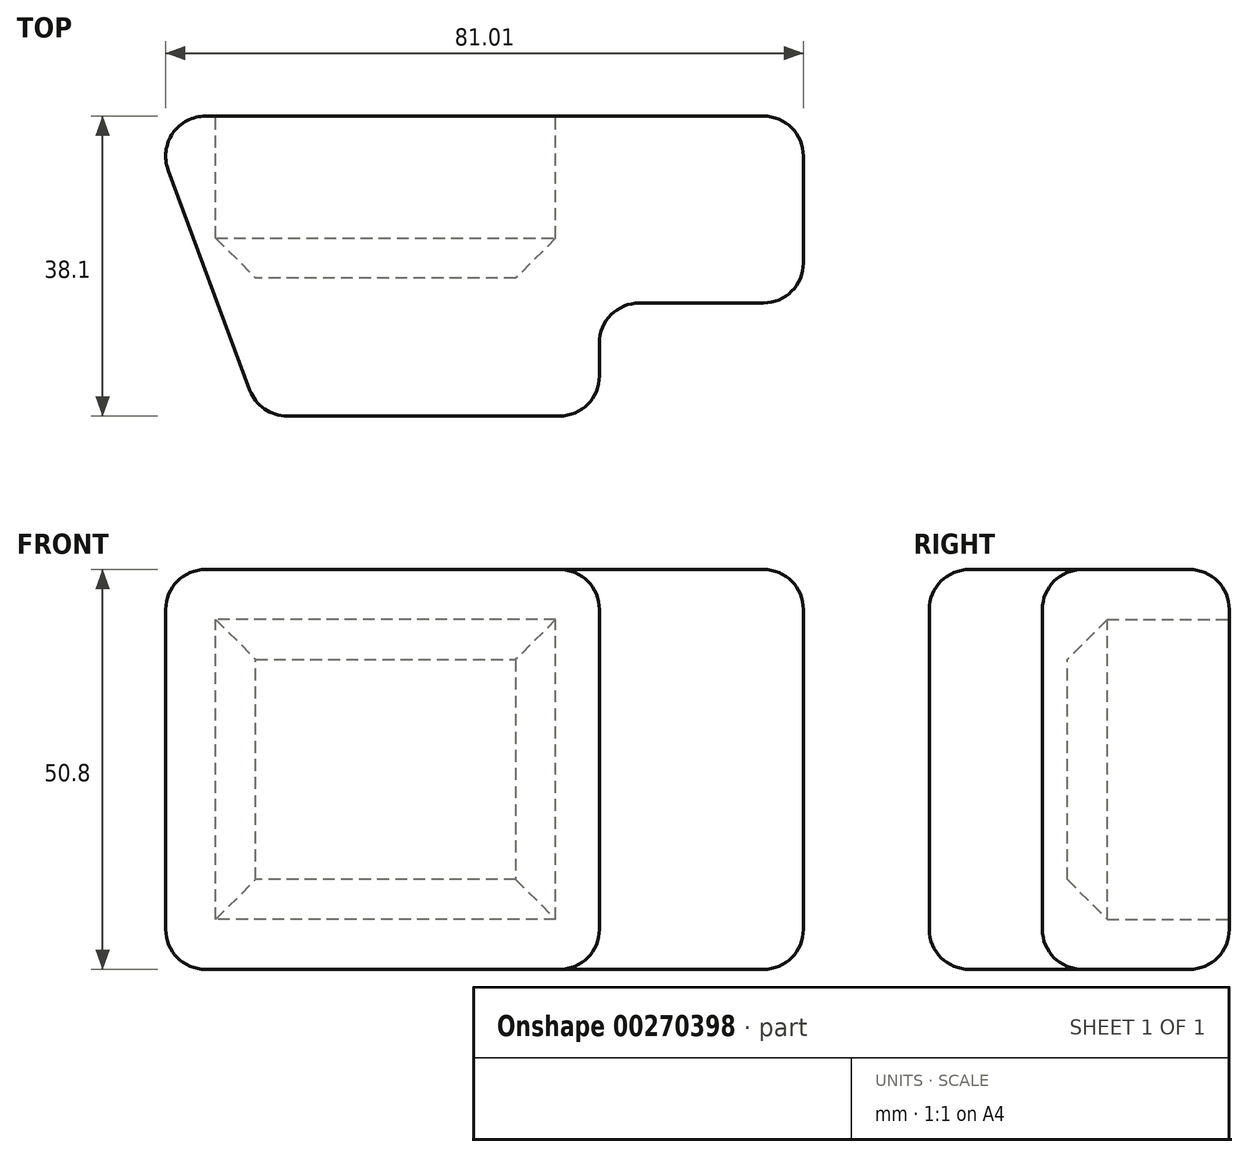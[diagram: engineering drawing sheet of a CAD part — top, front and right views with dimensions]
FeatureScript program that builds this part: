
annotation { "Feature Type Name" : "Feature", "Feature Type Description" : "" }
export const myFeature = defineFeature(function(context is Context, id is Id, definition is map)
    precondition{}
    {
        {
            var Q0;
            Q0=qCreatedBy(makeId("Top.planeOp"),FACE);
            var sketch = newSketch(context, id + "F0", { "sketchPlane" : qUnion([Q0])});
            skLineSegment(sketch, "E0", {"start": v(-35.45, 21) * mm, "end": v(-21.31, -17.1) * mm});
            skLineSegment(sketch, "E1", {"start": v(-21.31, -17.1) * mm, "end": v(21.87, -17.1) * mm});
            skLineSegment(sketch, "E2", {"start": v(21.87, -17.1) * mm, "end": v(21.87, 21) * mm});
            skLineSegment(sketch, "E3", {"start": v(21.87, 21) * mm, "end": v(-35.45, 21) * mm});
            skSolve(sketch);
        }
        {
            var Q0;
            Q0=makeQuery(id+"F0.imprint","IMPRINT",FACE,{"disambiguationData":[TD([[makeQuery(id+"F0.imprint","IMPRINT",EDGE,{"derivedFrom":sQuery(id+"F0.wireOp",EDGE,"E0")}),1.0]])]});
            extrude(context, id + "F1", {"entities" : qUnion([Q0]), "endBound" : BoundingType.SYMMETRIC, "depth" : 50.8 * mm});
        }
        {
            var Q0;
            Q0=makeQuery(id+"F1.opExtrude","SWEPT_FACE",FACE,{"disambiguationData":[OSD([sQuery(id+"F0.wireOp",EDGE,"E3")])]});
            var sketch = newSketch(context, id + "F2", { "sketchPlane" : qUnion([Q0])});
            skLineSegment(sketch, "E4.bottom", {"start": v(-16.32, -19.05) * mm, "end": v(26.86, -19.05) * mm});
            skLineSegment(sketch, "E4.top", {"start": v(-16.32, 19.05) * mm, "end": v(26.86, 19.05) * mm});
            skLineSegment(sketch, "E4.left", {"start": v(-16.32, -19.05) * mm, "end": v(-16.32, 19.05) * mm});
            skLineSegment(sketch, "E4.right", {"start": v(26.86, -19.05) * mm, "end": v(26.86, 19.05) * mm});
            skPoint(sketch, "E4.middle", {"position": v(5.27, 0) * mm});
            skSolve(sketch);
        }
        {
            var Q0;
            Q0 = qSketchRegion(id + "F2", true);
            extrude(context, id + "F3", {"entities" : qUnion([Q0]), "operationType" : NewBodyOperationType.REMOVE, "oppositeDirection" : true, "depth" : 20.57 * mm});
        }
        {
            var Q0;
            Q0=makeQuery(id+"F1.opExtrude","SWEPT_FACE",FACE,{"disambiguationData":[OSD([sQuery(id+"F0.wireOp",EDGE,"E2")])]});
            var sketch = newSketch(context, id + "F4", { "sketchPlane" : qUnion([Q0])});
            skLineSegment(sketch, "E5.bottom", {"start": v(21, -25.4) * mm, "end": v(-2.75, -25.4) * mm});
            skLineSegment(sketch, "E5.top", {"start": v(21, 25.4) * mm, "end": v(-2.75, 25.4) * mm});
            skLineSegment(sketch, "E5.left", {"start": v(21, -25.4) * mm, "end": v(21, 25.4) * mm});
            skLineSegment(sketch, "E5.right", {"start": v(-2.75, -25.4) * mm, "end": v(-2.75, 25.4) * mm});
            skPoint(sketch, "E5.middle", {"position": v(9.13, 0) * mm});
            skSolve(sketch);
        }
        {
            var Q0;
            Q0 = qSketchRegion(id + "F4", true);
            extrude(context, id + "F5", {"entities" : qUnion([Q0]), "operationType" : NewBodyOperationType.ADD, "depth" : 25.9 * mm});
        }
        {
            var Q0;
            Q0=makeQuery(id+"F5.boolean.opBoolean","MERGE",FACE,{"derivedFrom":[makeQuery(id+"F1.opExtrude","SWEPT_FACE",FACE,{"disambiguationData":[OSD([sQuery(id+"F0.wireOp",EDGE,"E3")])]}),makeQuery(id+"F5.opExtrude","SWEPT_FACE",FACE,{"disambiguationData":[OSD([sQuery(id+"F4.wireOp",EDGE,"E5.left")])]})]});
            var sketch = newSketch(context, id + "F6", { "sketchPlane" : qUnion([Q0])});
            skLineSegment(sketch, "E6", {"start": v(-47.78, 0) * mm, "end": v(-16.32, 0) * mm});
            skPoint(sketch, "E7", {"position": v(-32.05, 0) * mm});
            skPoint(sketch, "E8", {"position": v(-28.64, 14.84) * mm});
            skPoint(sketch, "E9.MirrorP", {"position": v(-28.64, -14.84) * mm});
            skSolve(sketch);
        }
        {
            var Q0;
            Q0=makeQuery(id+"F5.opExtrude","SWEPT_EDGE",EDGE,{"disambiguationData":[OSD([sQuery(id+"F0.wireOp",EDGE,"E2"),sQuery(id+"F4.wireOp",EDGE,"E5.top"),sQuery(id+"F4.wireOp",EDGE,"E5.right")])]});
            var Q1;
            Q1=makeQuery(id+"F5.opExtrude","CAP_EDGE",EDGE,{"disambiguationData":[OSD([sQuery(id+"F4.wireOp",EDGE,"E5.top")])],"isStart":false});
            var Q2;
            Q2=makeQuery(id+"F5.opExtrude","CAP_EDGE",EDGE,{"disambiguationData":[OSD([sQuery(id+"F4.wireOp",EDGE,"E5.right")])],"isStart":false});
            var Q3;
            Q3=makeQuery(id+"F5.opExtrude","CAP_EDGE",EDGE,{"disambiguationData":[OSD([sQuery(id+"F4.wireOp",EDGE,"E5.bottom")])],"isStart":false});
            var Q4;
            Q4=makeQuery(id+"F5.opExtrude","SWEPT_EDGE",EDGE,{"disambiguationData":[OSD([sQuery(id+"F0.wireOp",EDGE,"E2"),sQuery(id+"F4.wireOp",EDGE,"E5.bottom"),sQuery(id+"F4.wireOp",EDGE,"E5.right")])]});
            var Q5;
            Q5=makeQuery(id+"F5.opExtrude","CAP_EDGE",EDGE,{"disambiguationData":[OSD([sQuery(id+"F4.wireOp",EDGE,"E5.left")])],"isStart":false});
            var Q6;
            Q6=makeQuery(id+"F1.opExtrude","CAP_EDGE",EDGE,{"disambiguationData":[OSD([sQuery(id+"F0.wireOp",EDGE,"E2")])],"isStart":false});
            var Q7;
            Q7=makeQuery(id+"F1.opExtrude","SWEPT_FACE",FACE,{"disambiguationData":[OSD([sQuery(id+"F0.wireOp",EDGE,"E2")])]});
            fillet(context, id + "F7", {"entities" : qUnion([Q0, Q1, Q2, Q3, Q4, Q5, Q6, Q7]), "radius" : 5.08 * mm, "tangentPropagation" : true, "allowEdgeOverflow" : false});
        }
        {
            var Q0;
            Q0=makeQuery(id+"F1.opExtrude","CAP_EDGE",EDGE,{"disambiguationData":[OSD([sQuery(id+"F0.wireOp",EDGE,"E1")])],"isStart":false});
            var Q1;
            Q1=makeQuery(id+"F1.opExtrude","CAP_EDGE",EDGE,{"disambiguationData":[OSD([sQuery(id+"F0.wireOp",EDGE,"E0")])],"isStart":false});
            var Q2;
            Q2=makeQuery(id+"F5.boolean.opBoolean","MERGE",EDGE,{"derivedFrom":[makeQuery(id+"F1.opExtrude","CAP_EDGE",EDGE,{"disambiguationData":[OSD([sQuery(id+"F0.wireOp",EDGE,"E3")])],"isStart":false}),makeQuery(id+"F5.opExtrude","SWEPT_EDGE",EDGE,{"disambiguationData":[OSD([sQuery(id+"F4.wireOp",EDGE,"E5.top"),sQuery(id+"F4.wireOp",EDGE,"E5.left")])]})]});
            var Q3;
            Q3=makeQuery(id+"F5.boolean.opBoolean","MERGE",FACE,{"derivedFrom":[makeQuery(id+"F1.opExtrude","CAP_FACE",FACE,{"disambiguationData":[OSD([sQuery(id+"F0.wireOp",EDGE,"E0"),sQuery(id+"F0.wireOp",EDGE,"E1"),sQuery(id+"F0.wireOp",EDGE,"E2"),sQuery(id+"F0.wireOp",EDGE,"E3")])],"isStart":true}),makeQuery(id+"F5.opExtrude","SWEPT_FACE",FACE,{"disambiguationData":[OSD([sQuery(id+"F4.wireOp",EDGE,"E5.bottom")])]})]});
            var Q4;
            Q4=makeQuery(id+"F1.opExtrude","SWEPT_EDGE",EDGE,{"disambiguationData":[OSD([sQuery(id+"F0.wireOp",EDGE,"E0"),sQuery(id+"F0.wireOp",EDGE,"E3")])]});
            var Q5;
            Q5=makeQuery(id+"F1.opExtrude","SWEPT_EDGE",EDGE,{"disambiguationData":[OSD([sQuery(id+"F0.wireOp",EDGE,"E0"),sQuery(id+"F0.wireOp",EDGE,"E1")])]});
            fillet(context, id + "F8", {"entities" : qUnion([Q0, Q1, Q2, Q3, Q4, Q5]), "radius" : 5.08 * mm, "tangentPropagation" : true, "allowEdgeOverflow" : false});
        }
        {
            var Q0;
            Q0=makeQuery(id+"F3.boolean.opBoolean","COPY",EDGE,{"derivedFrom":makeQuery(id+"F3.opExtrude","CAP_EDGE",EDGE,{"disambiguationData":[OSD([sQuery(id+"F2.wireOp",EDGE,"E4.left")])],"isStart":false})});
            var Q1;
            Q1=makeQuery(id+"F3.boolean.opBoolean","COPY",EDGE,{"derivedFrom":makeQuery(id+"F3.opExtrude","CAP_EDGE",EDGE,{"disambiguationData":[OSD([sQuery(id+"F2.wireOp",EDGE,"E4.top")])],"isStart":false})});
            var Q2;
            Q2=makeQuery(id+"F3.boolean.opBoolean","COPY",EDGE,{"derivedFrom":makeQuery(id+"F3.opExtrude","CAP_EDGE",EDGE,{"disambiguationData":[OSD([sQuery(id+"F2.wireOp",EDGE,"E4.bottom")])],"isStart":false})});
            var Q3;
            Q3=makeQuery(id+"F3.boolean.opBoolean","COPY",EDGE,{"derivedFrom":makeQuery(id+"F3.opExtrude","CAP_EDGE",EDGE,{"disambiguationData":[OSD([sQuery(id+"F2.wireOp",EDGE,"E4.right")])],"isStart":false})});
            chamfer(context, id + "F9", {"entities" : qUnion([Q0, Q1, Q2, Q3]), "width" : 5.08 * mm, "tangentPropagation" : true});
        }
    });
